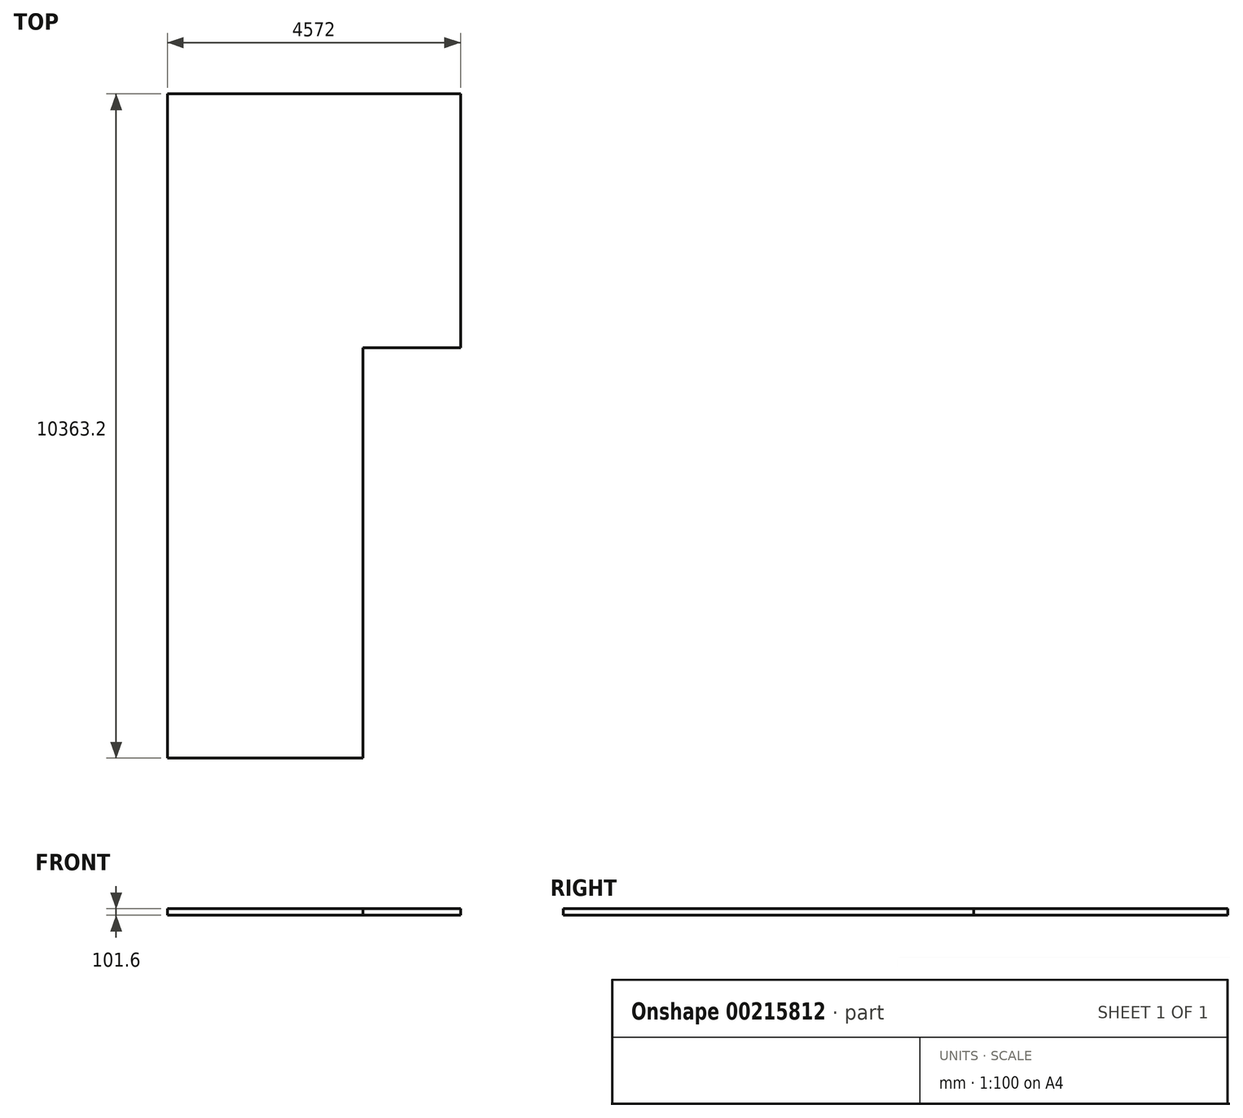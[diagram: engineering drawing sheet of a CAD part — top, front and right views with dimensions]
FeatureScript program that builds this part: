
annotation { "Feature Type Name" : "Feature", "Feature Type Description" : "" }
export const myFeature = defineFeature(function(context is Context, id is Id, definition is map)
    precondition{}
    {
        {
            var Q0;
            Q0=qCreatedBy(makeId("Top.planeOp"),FACE);
            var sketch = newSketch(context, id + "F0", { "sketchPlane" : qUnion([Q0])});
            skLineSegment(sketch, "E0.bottom", {"start": v(-2102.65, -5186.4) * mm, "end": v(945.35, -5186.4) * mm});
            skLineSegment(sketch, "E0.top", {"start": v(-2102.65, 5176.8) * mm, "end": v(945.35, 5176.8) * mm});
            skLineSegment(sketch, "E0.left", {"start": v(-2102.65, -5186.4) * mm, "end": v(-2102.65, 5176.8) * mm});
            skLineSegment(sketch, "E0.right", {"start": v(945.35, -5186.4) * mm, "end": v(945.35, 5176.8) * mm});
            skLineSegment(sketch, "E1.bottom", {"start": v(945.35, 1214.4) * mm, "end": v(2469.35, 1214.4) * mm});
            skLineSegment(sketch, "E1.top", {"start": v(945.35, 5176.8) * mm, "end": v(2469.35, 5176.8) * mm});
            skLineSegment(sketch, "E1.left", {"start": v(945.35, 1214.4) * mm, "end": v(945.35, 5176.8) * mm});
            skLineSegment(sketch, "E1.right", {"start": v(2469.35, 1214.4) * mm, "end": v(2469.35, 5176.8) * mm});
            skSolve(sketch);
        }
        {
            var Q0;
            Q0 = qSketchRegion(id + "F0", true);
            extrude(context, id + "F1", {"entities" : qUnion([Q0]), "oppositeDirection" : true, "depth" : 101.6 * mm});
        }
    });
